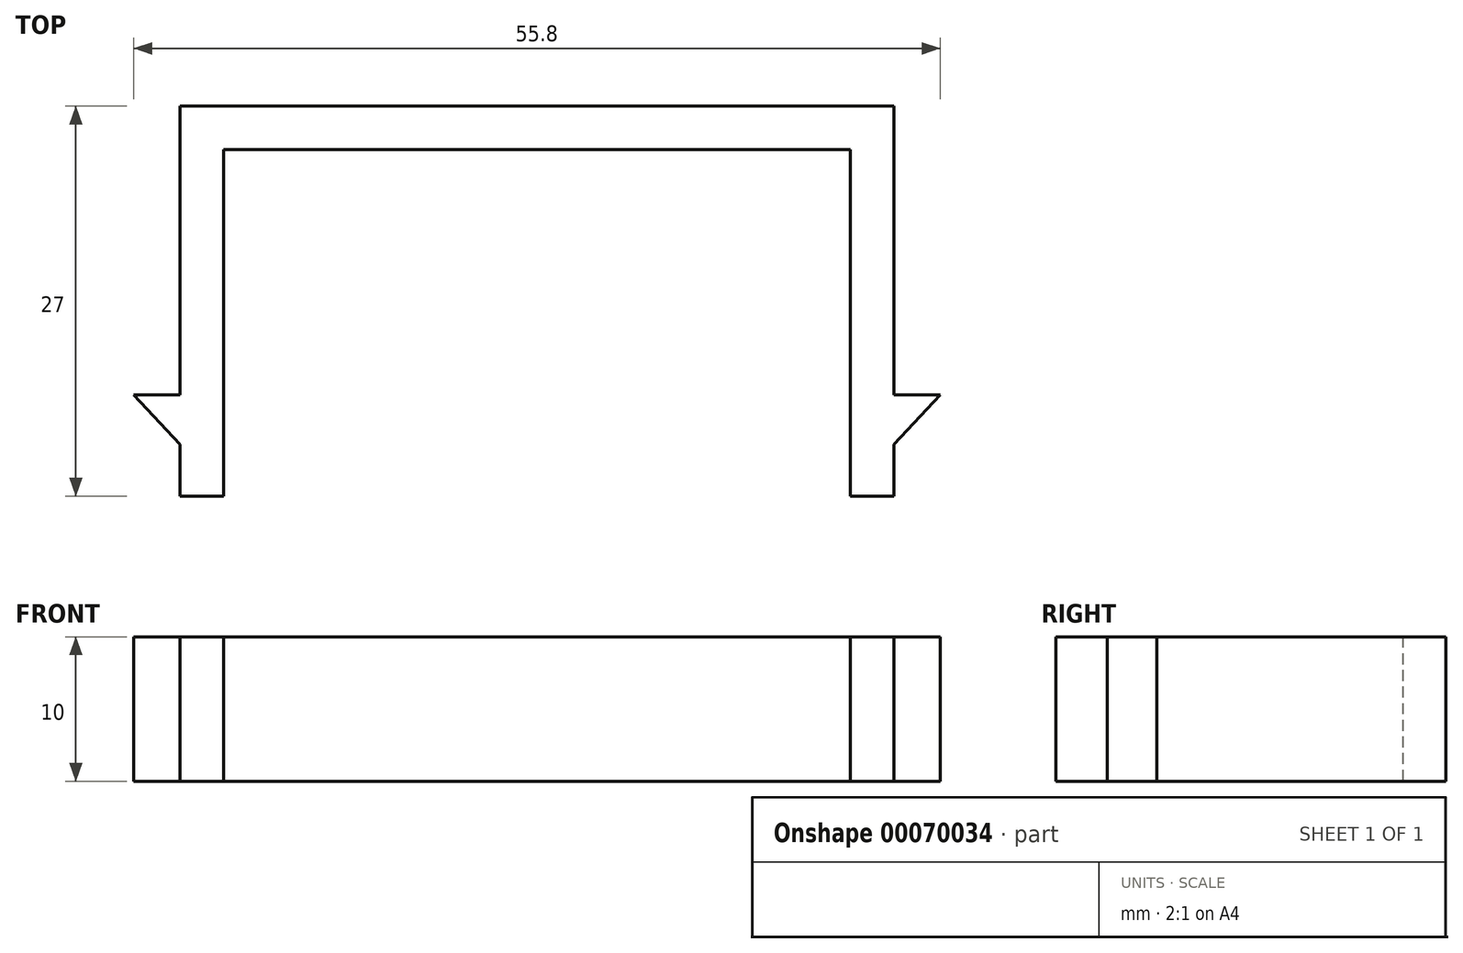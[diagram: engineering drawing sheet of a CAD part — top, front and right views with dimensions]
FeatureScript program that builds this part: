
annotation { "Feature Type Name" : "Feature", "Feature Type Description" : "" }
export const myFeature = defineFeature(function(context is Context, id is Id, definition is map)
    precondition{}
    {
        {
            var Q0;
            Q0=qCreatedBy(makeId("Top.planeOp"),FACE);
            var sketch = newSketch(context, id + "F0", { "sketchPlane" : qUnion([Q0])});
            skLineSegment(sketch, "E0", {"start": v(0, 14) * mm, "end": v(-24.7, 14) * mm});
            skLineSegment(sketch, "E1", {"start": v(-24.7, -13) * mm, "end": v(-21.7, -13) * mm});
            skLineSegment(sketch, "E2", {"start": v(-21.7, -13) * mm, "end": v(-21.7, 11) * mm});
            skLineSegment(sketch, "E3", {"start": v(-24.7, -6) * mm, "end": v(-27.9, -6) * mm});
            skLineSegment(sketch, "E4", {"start": v(-27.9, -6) * mm, "end": v(-24.7, -9.43) * mm});
            skLineSegment(sketch, "E5", {"start": v(0, 18.97) * mm, "end": v(0, -27.48) * mm, "construction": true});
            skLineSegment(sketch, "E6", {"start": v(-24.7, 14) * mm, "end": v(-24.7, -6) * mm});
            skLineSegment(sketch, "E7", {"start": v(-24.7, -9.43) * mm, "end": v(-24.7, -13) * mm});
            skLineSegment(sketch, "E8", {"start": v(-21.7, 11) * mm, "end": v(0, 11) * mm});
            skLineSegment(sketch, "E9.MirrorCS", {"start": v(0, 14) * mm, "end": v(24.7, 14) * mm});
            skLineSegment(sketch, "E10.MirrorCS", {"start": v(21.7, 11) * mm, "end": v(0, 11) * mm});
            skLineSegment(sketch, "E11.MirrorCS", {"start": v(24.7, 14) * mm, "end": v(24.7, -6) * mm});
            skLineSegment(sketch, "E12.MirrorCS", {"start": v(21.7, -13) * mm, "end": v(21.7, 11) * mm});
            skLineSegment(sketch, "E13.MirrorCS", {"start": v(24.7, -6) * mm, "end": v(27.9, -6) * mm});
            skLineSegment(sketch, "E14.MirrorCS", {"start": v(27.9, -6) * mm, "end": v(24.7, -9.43) * mm});
            skLineSegment(sketch, "E15.MirrorCS", {"start": v(24.7, -9.43) * mm, "end": v(24.7, -13) * mm});
            skLineSegment(sketch, "E16.MirrorCS", {"start": v(24.7, -13) * mm, "end": v(21.7, -13) * mm});
            skSolve(sketch);
        }
        {
            var Q0;
            Q0=makeQuery(id+"F0.imprint","IMPRINT",FACE,{"disambiguationData":[TD([[makeQuery(id+"F0.imprint","IMPRINT",EDGE,{"derivedFrom":sQuery(id+"F0.wireOp",EDGE,"E0")}),1.0]])]});
            extrude(context, id + "F1", {"entities" : qUnion([Q0]), "depth" : 10 * mm});
        }
    });
